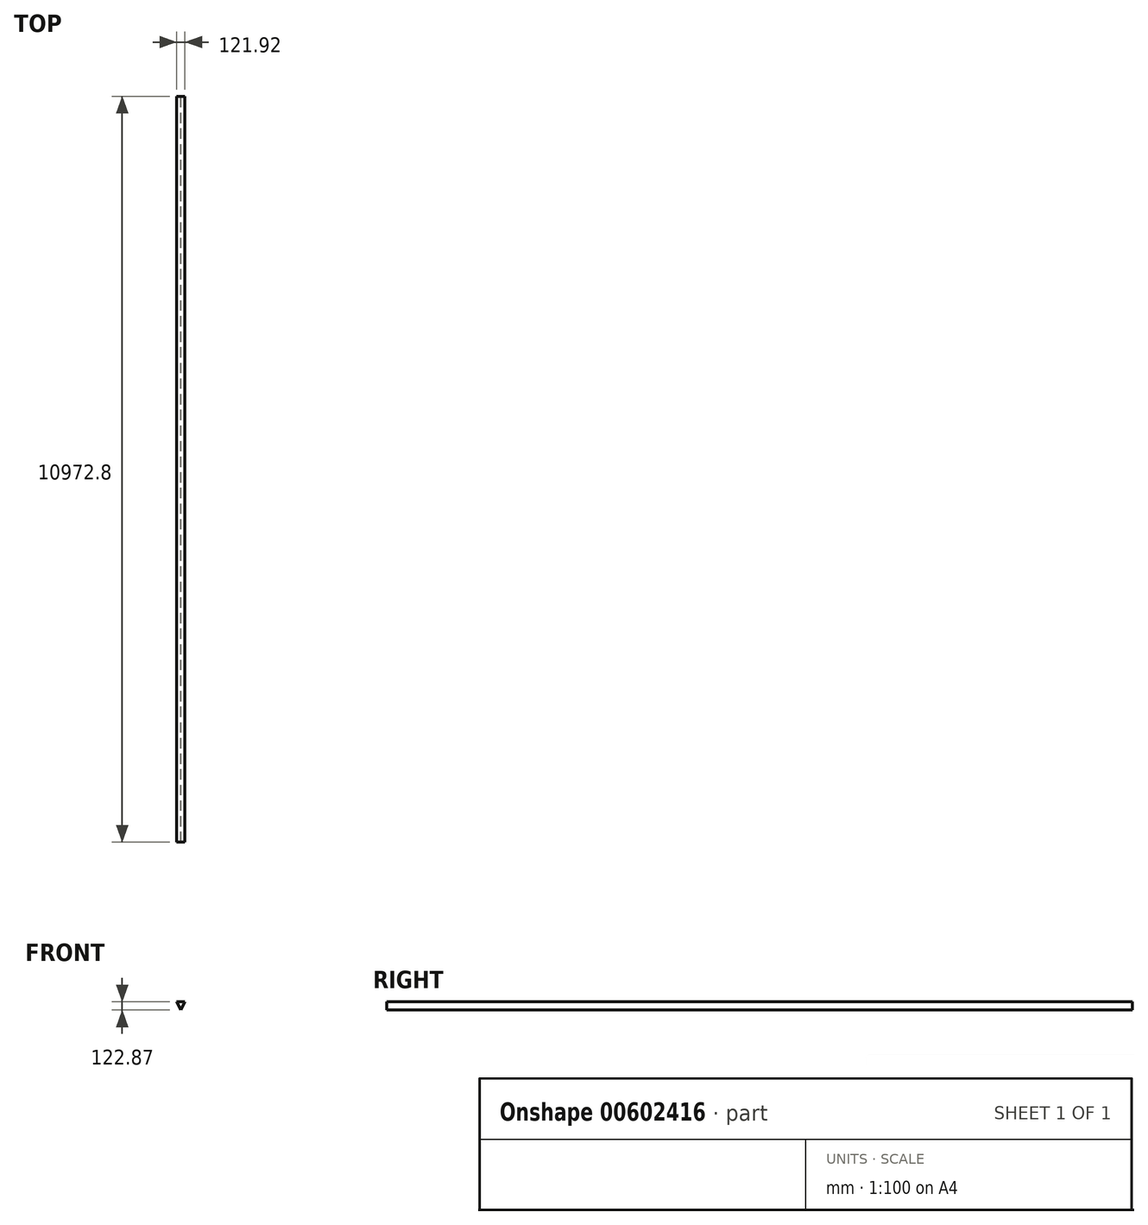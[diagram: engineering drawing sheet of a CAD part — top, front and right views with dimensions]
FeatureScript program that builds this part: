
annotation { "Feature Type Name" : "Feature", "Feature Type Description" : "" }
export const myFeature = defineFeature(function(context is Context, id is Id, definition is map)
    precondition{}
    {
        {
            var Q0;
            Q0=qCreatedBy(makeId("Front.planeOp"),FACE);
            var sketch = newSketch(context, id + "F0", { "sketchPlane" : qUnion([Q0])});
            skLineSegment(sketch, "E0", {"start": v(0, 0) * mm, "end": v(-60.96, 122.87) * mm});
            skLineSegment(sketch, "E1", {"start": v(-60.96, 122.87) * mm, "end": v(60.96, 122.87) * mm});
            skLineSegment(sketch, "E2", {"start": v(60.96, 122.87) * mm, "end": v(0, 0) * mm});
            skSolve(sketch);
        }
        {
            var Q0;
            Q0=makeQuery(id+"F0.imprint","IMPRINT",FACE,{"disambiguationData":[TD([[makeQuery(id+"F0.imprint","IMPRINT",EDGE,{"derivedFrom":sQuery(id+"F0.wireOp",EDGE,"E0")}),-1.0]])]});
            extrude(context, id + "F1", {"entities" : qUnion([Q0]), "depth" : 10972.8 * mm, "offsetDistance" : 30.48 * mm});
        }
    });
